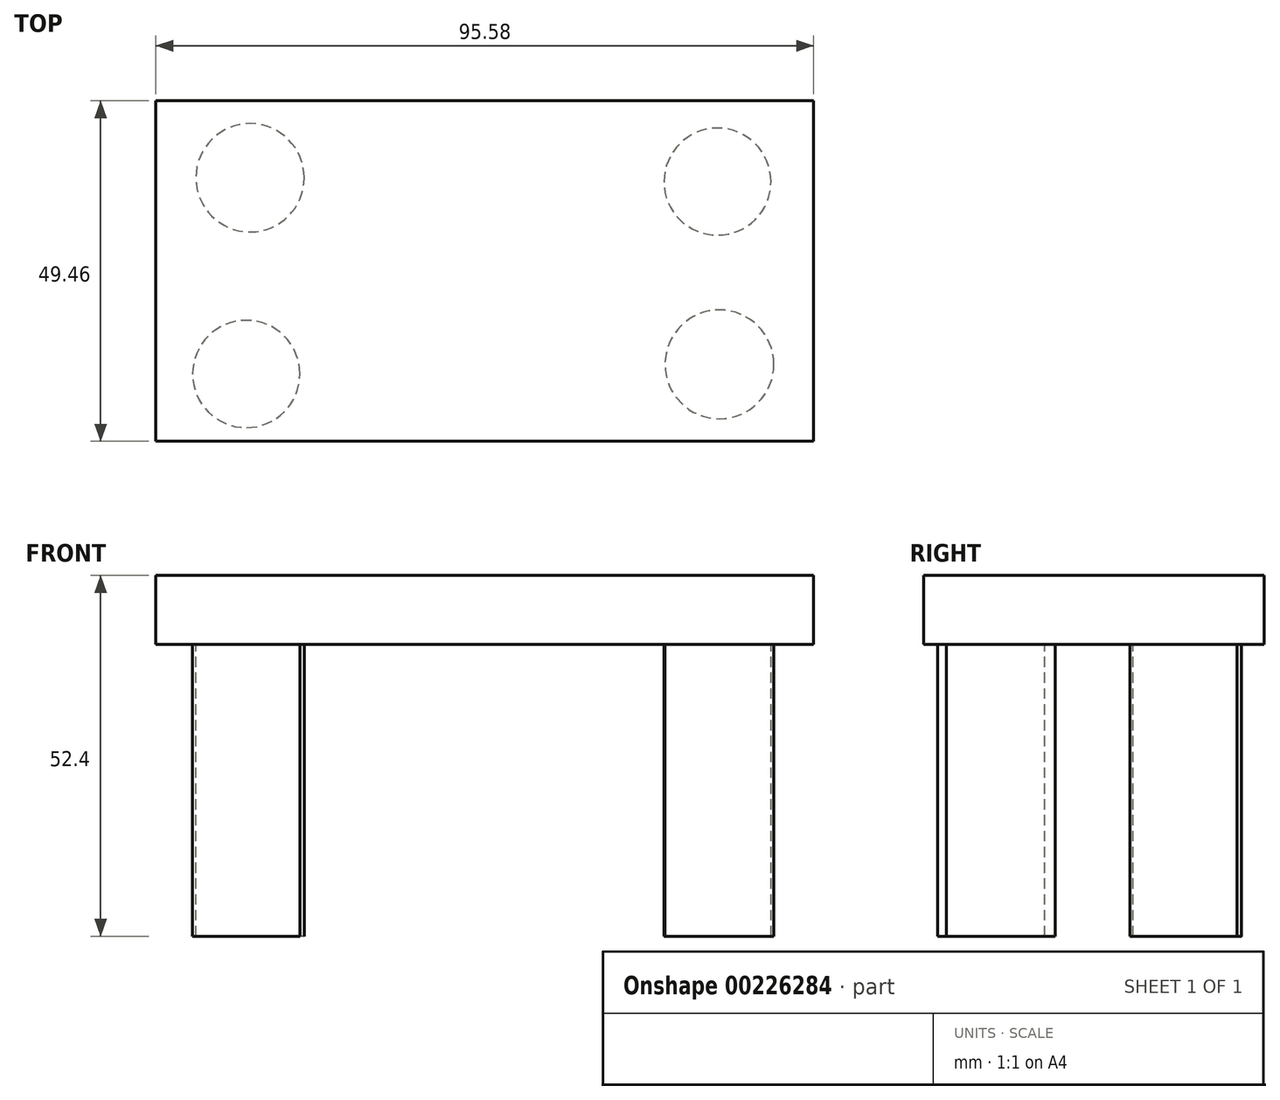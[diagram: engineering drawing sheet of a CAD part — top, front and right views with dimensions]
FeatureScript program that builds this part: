
annotation { "Feature Type Name" : "Feature", "Feature Type Description" : "" }
export const myFeature = defineFeature(function(context is Context, id is Id, definition is map)
    precondition{}
    {
        {
            var Q0;
            Q0=qCreatedBy(makeId("Top.planeOp"),FACE);
            var sketch = newSketch(context, id + "F0", { "sketchPlane" : qUnion([Q0])});
            skLineSegment(sketch, "E0.bottom", {"start": v(47.79, 24.73) * mm, "end": v(-47.79, 24.73) * mm});
            skLineSegment(sketch, "E0.top", {"start": v(47.79, -24.73) * mm, "end": v(-47.79, -24.73) * mm});
            skLineSegment(sketch, "E0.left", {"start": v(47.79, 24.73) * mm, "end": v(47.79, -24.73) * mm});
            skLineSegment(sketch, "E0.right", {"start": v(-47.79, 24.73) * mm, "end": v(-47.79, -24.73) * mm});
            skPoint(sketch, "E0.middle", {"position": v(0, 0) * mm});
            skCircle(sketch, "E1", {"center": v(-34.1, 13.55) * mm, "radius": 7.87 * mm});
            skCircle(sketch, "E2", {"center": v(-34.65, -14.95) * mm, "radius": 7.8 * mm});
            skCircle(sketch, "E3", {"center": v(33.82, 13) * mm, "radius": 7.77 * mm});
            skCircle(sketch, "E4", {"center": v(34.1, -13.55) * mm, "radius": 7.9 * mm});
            skSolve(sketch);
        }
        {
            var Q0;
            Q0=makeQuery(id+"F0.imprint","IMPRINT",FACE,{"disambiguationData":[TD([[makeQuery(id+"F0.imprint","IMPRINT",EDGE,{"derivedFrom":sQuery(id+"F0.wireOp",EDGE,"E0.bottom")}),1.0]])]});
            var Q1;
            Q1=makeQuery(id+"F0.imprint","IMPRINT",FACE,{"disambiguationData":[TD([[makeQuery(id+"F0.imprint","IMPRINT",EDGE,{"derivedFrom":sQuery(id+"F0.wireOp",EDGE,"E2")}),1.0]])]});
            var Q2;
            Q2=makeQuery(id+"F0.imprint","IMPRINT",FACE,{"disambiguationData":[TD([[makeQuery(id+"F0.imprint","IMPRINT",EDGE,{"derivedFrom":sQuery(id+"F0.wireOp",EDGE,"E1")}),1.0]])]});
            var Q3;
            Q3=makeQuery(id+"F0.imprint","IMPRINT",FACE,{"disambiguationData":[TD([[makeQuery(id+"F0.imprint","IMPRINT",EDGE,{"derivedFrom":sQuery(id+"F0.wireOp",EDGE,"E4")}),1.0]])]});
            var Q4;
            Q4=makeQuery(id+"F0.imprint","IMPRINT",FACE,{"disambiguationData":[TD([[makeQuery(id+"F0.imprint","IMPRINT",EDGE,{"derivedFrom":sQuery(id+"F0.wireOp",EDGE,"E3")}),1.0]])]});
            extrude(context, id + "F1", {"entities" : qUnion([Q0, Q1, Q2, Q3, Q4]), "depth" : 10 * mm});
        }
        {
            var Q0;
            Q0=makeQuery(id+"F0.imprint","IMPRINT",FACE,{"disambiguationData":[TD([[makeQuery(id+"F0.imprint","IMPRINT",EDGE,{"derivedFrom":sQuery(id+"F0.wireOp",EDGE,"E2")}),1.0]])]});
            var Q1;
            Q1=makeQuery(id+"F0.imprint","IMPRINT",FACE,{"disambiguationData":[TD([[makeQuery(id+"F0.imprint","IMPRINT",EDGE,{"derivedFrom":sQuery(id+"F0.wireOp",EDGE,"E4")}),1.0]])]});
            var Q2;
            Q2=makeQuery(id+"F0.imprint","IMPRINT",FACE,{"disambiguationData":[TD([[makeQuery(id+"F0.imprint","IMPRINT",EDGE,{"derivedFrom":sQuery(id+"F0.wireOp",EDGE,"E3")}),1.0]])]});
            var Q3;
            Q3=makeQuery(id+"F0.imprint","IMPRINT",FACE,{"disambiguationData":[TD([[makeQuery(id+"F0.imprint","IMPRINT",EDGE,{"derivedFrom":sQuery(id+"F0.wireOp",EDGE,"E1")}),1.0]])]});
            extrude(context, id + "F2", {"entities" : qUnion([Q0, Q1, Q2, Q3]), "operationType" : NewBodyOperationType.ADD, "oppositeDirection" : true, "depth" : 42.4 * mm});
        }
    });
